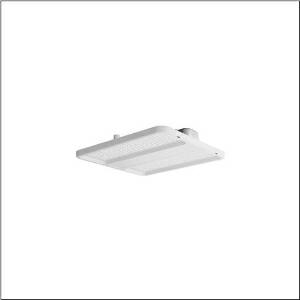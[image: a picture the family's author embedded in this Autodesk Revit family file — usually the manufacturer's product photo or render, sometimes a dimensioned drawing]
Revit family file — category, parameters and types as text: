
# Revit family: highbay_21_midi_52hn11da4lda
name_source: partatom
category: Lighting Fixtures
units: mm (PartAtom-declared; Revit-internal decimal feet)

## family parameters
Cut with Voids When Loaded = No
Host = Face
Light Source = No
Part Type = Normal
Room Calculation Point = No
Round Connector Dimension = Use Diameter
Shared = No

## types (1)
- --- (1 x LED, 4160 lm, 22.3 W, 4000K)
    Apparent Load = 22 VA
    CIE Flux Codes = 89 97 99 100 100
    Color Rendering = 80
    Color Temperature = 4000K
    Default Elevation = 1800 mm
    Description = high bay luminaire Highbay 21 midi; direct symmetric narrow distribution, light control with lens of PMMA; UGR ≤ 22 (X = 4H | Y = 8H | S = 0.25H | reflection values 70/50/20); luminous flux: 26.500lm; light colour: 840, colour temperature: 4000K, MacAdam ≤ 3 SDCM (initial), colour rendering: CRI > 80; luminous efficacy: 185,8lm/W; rated service life: 75.000h (L80/B50) at AT= ta max; control: DALI 2; housing frame of high-performance plastic PA6, matt traffic white (RAL 9016); cover of PMMA; dimension (LxWxH): 474 x 442 x 72mm; luminaire connection: terminal, 5-pole, max. 2.5mm² (cable entry for one cable, Ø 8.5..16mm); mains connection: 230..240V, AC/DC 0/50..60Hz; connected load: 142,6W; protection rating (complete): IP66; insulation class (complete): insulation class I (protective earthing); protection symbol: D; impact resistance: IK08; halogen-free wiring; for central battery installations according to DIN EN 60598-2-22; LABS conformity tested according to VDMA 24364:2018-05; corresponds to IFS (International Featured Standards) requirements for safety and quality in the food industry; certification: CE, ENEC, VDE, UKCA; permissible operating ambient temperature: -40..+55°C (reducing of maximum allowable ambient temperature of 5°C with ceiling mounting); packaging unit: 1 piece; (delivery without accessories; please order mounting accessories separately)
    Height = 72 mm  [stored 0.23622 ft]
    Lamp = 1 x LED
    Lamp Light Flux = 4160 lm
    Lamp Power = 22.3 W
    Lamp count = 1
    Length = 474 mm
    Luminous efficacy = 187 lm/W
    Manufacturer = Siteco
    ModVariant = No
    Model = 52HN11DA4LDA
    Mounting Place = Ceiling
    Mounting Type = Pendant
    Number of Poles = 1
    OnlyDefault = Yes
    Power Factor = 1
    Product Name = Highbay 21 midi
    Product group = high bay luminaire
    ProductGroupID = 901
    Protection Class = Protection class I
    Protection Degree = IP 66
    RLX_Detail_Level = 1
    RLX_Emergency_Light_Flux = 0 lm
    RLX_Emergency_Type = 0
    RLX_Emergency_Type_DB = No
    RlxData = <blob elided: 17633 chars, md5=26f8075b>
    Socket = socket
    Standby Power = 0 W
    System Light Flux = 4160 lm
    System Power = 22 W
    Type Comments = : DC mode (central or group accumulator) initial emergency light level
    Type Image = l_1363240.jpg
    URL = http://relux.com
    VarID = @adj_000175
    Voltage = 0 V
    Weight = 0.00 kg
    Width = 442 mm

note: [stored X ft] marks values corroborated as IEEE doubles in the binary element streams (Revit-internal decimal feet)

## geometry (parser evidence)
native form markers: Blend x4, Sweep x12
no freeform markers — native parametric forms only
